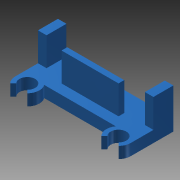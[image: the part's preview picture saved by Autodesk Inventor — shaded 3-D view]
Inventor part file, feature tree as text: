
AUTODESK INVENTOR PART (.ipt)
format: ipt  version: 2013 (Build 170138000, 138)  size: 133,120 bytes
history: native  units: mm
features: extrude x3, sketch x3
ambient origin geometry x8: Origin, YZ Plane, XZ Plane, XY Plane, X Axis, Y Axis, Z Axis, Center Point
bodies: Solid1 (feature_tree)
feature tree (6):
  extrude  "Extrusion1"  Depth=15.0mm
  extrude  "Extrusion2"  Depth=1.5mm
  extrude  "Extrusion3"  Depth=4.0mm TaperAngle=0.0deg
  sketch  "Sketch1"  dims[d0=32.0mm d2=15.0mm]
  sketch  "Sketch2"  dims[d4=5.5mm d6=1.5mm]
  sketch  "Sketch3"  dims[d7=1.5mm d8=4.0mm d9=0.0mm d10=5.5mm d11=2.5mm d16=2.0mm d17=0.0mm d18=3.0mm d19=7.0mm d20=3.0mm d21=7.0mm d22=10.0mm d23=0.0mm d24=45.0deg d25=2.0mm d26=20.0mm]
